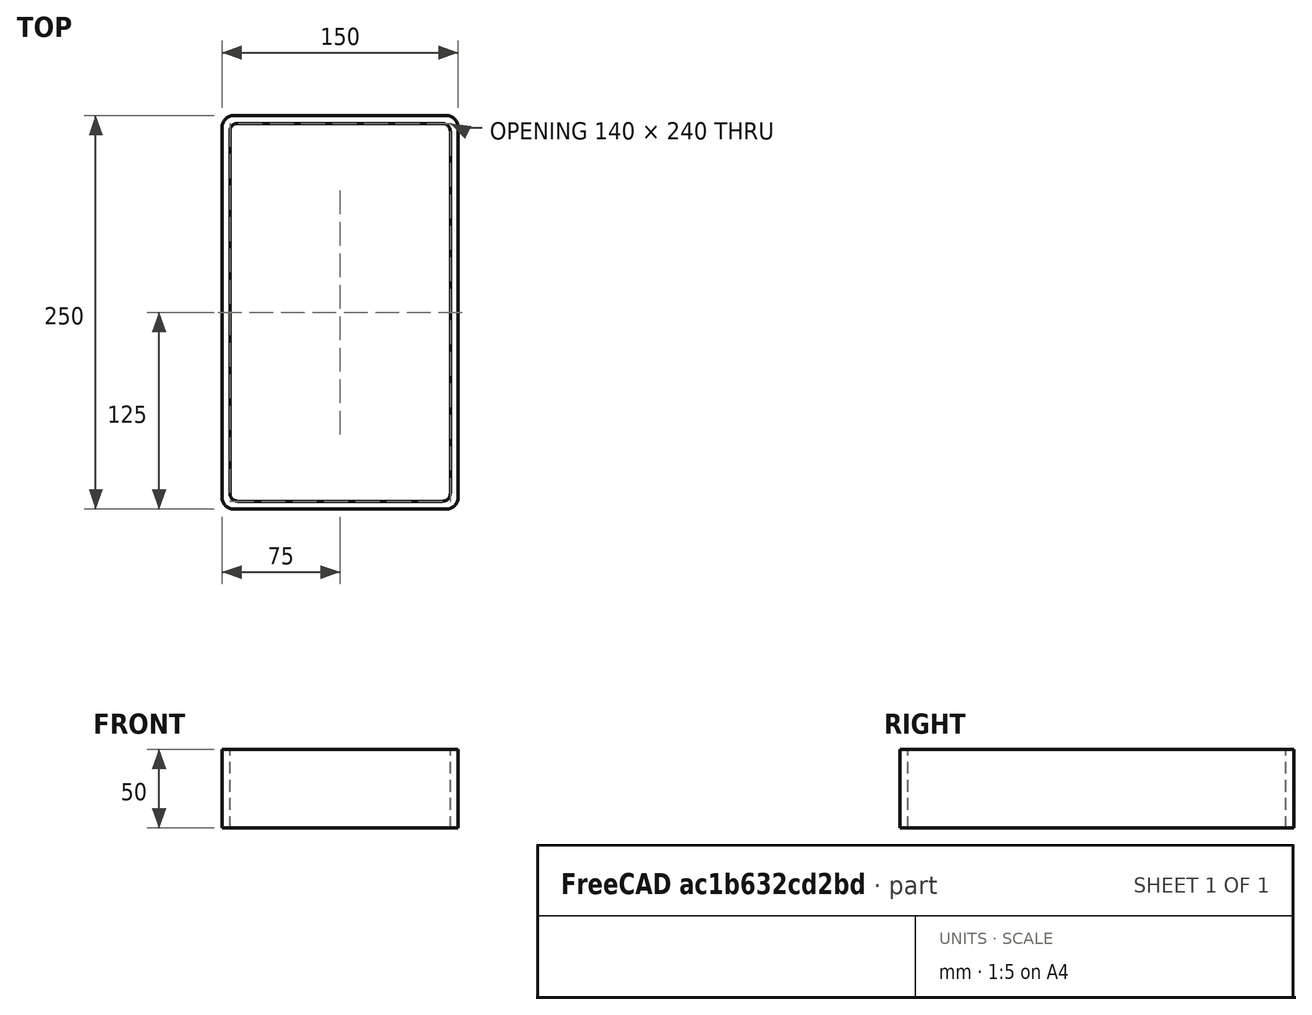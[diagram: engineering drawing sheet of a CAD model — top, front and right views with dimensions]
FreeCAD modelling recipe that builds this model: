
FCSTD DOCUMENT  (FreeCAD 0.15R4671 (Git))
Label: Rectangular hollow section 250x150x5 EN10219 S235JRH
License: All rights reserved
LicenseURL: http://en.wikipedia.org/wiki/All_rights_reserved
objects: Sketcher::SketchObject×1, Part::Extrusion×1
note: 2 computed .brp shape members not serialized (recipe doc carries the construction recipe); baked Part::Feature solids carry a one-line shape summary decoded from their .brp

FEATURE [Sketcher::SketchObject] Sketch
  sketch-geometry (16):
    g0: LineSegment StartX=-65 StartY=120 StartZ=0 EndX=65 EndY=120 EndZ=0
    g1: LineSegment StartX=70 StartY=115 StartZ=0 EndX=70 EndY=-115 EndZ=0
    g2: LineSegment StartX=65 StartY=-120 StartZ=0 EndX=-65 EndY=-120 EndZ=0
    g3: LineSegment StartX=-70 StartY=-115 StartZ=0 EndX=-70 EndY=115 EndZ=0
    g4: LineSegment StartX=-67.5 StartY=125 StartZ=0 EndX=67.5 EndY=125 EndZ=0
    g5: LineSegment StartX=75 StartY=117.5 StartZ=0 EndX=75 EndY=-117.5 EndZ=0
    g6: LineSegment StartX=67.5 StartY=-125 StartZ=0 EndX=-67.5 EndY=-125 EndZ=0
    g7: LineSegment StartX=-75 StartY=-117.5 StartZ=0 EndX=-75 EndY=117.5 EndZ=0
    g8: ArcOfCircle CenterX=-65 CenterY=115 CenterZ=0 NormalX=0 NormalY=0 NormalZ=1 Radius=5 StartAngle=1.5708 EndAngle=3.14159
    g9: ArcOfCircle CenterX=65 CenterY=115 CenterZ=0 NormalX=0 NormalY=0 NormalZ=1 Radius=5 StartAngle=0 EndAngle=1.5708
    g10: ArcOfCircle CenterX=65 CenterY=-115 CenterZ=0 NormalX=0 NormalY=0 NormalZ=1 Radius=5 StartAngle=4.71239 EndAngle=6.28319
    g11: ArcOfCircle CenterX=-65 CenterY=-115 CenterZ=0 NormalX=0 NormalY=0 NormalZ=1 Radius=5 StartAngle=3.14159 EndAngle=4.71239
    g12: ArcOfCircle CenterX=67.5 CenterY=117.5 CenterZ=0 NormalX=0 NormalY=0 NormalZ=1 Radius=7.5 StartAngle=0 EndAngle=1.5708
    g13: ArcOfCircle CenterX=67.5 CenterY=-117.5 CenterZ=0 NormalX=0 NormalY=0 NormalZ=1 Radius=7.5 StartAngle=4.71239 EndAngle=6.28319
    g14: ArcOfCircle CenterX=-67.5 CenterY=-117.5 CenterZ=0 NormalX=0 NormalY=0 NormalZ=1 Radius=7.5 StartAngle=3.14159 EndAngle=4.71239
    g15: ArcOfCircle CenterX=-67.5 CenterY=117.5 CenterZ=0 NormalX=0 NormalY=0 NormalZ=1 Radius=7.5 StartAngle=1.5708 EndAngle=3.14159
  constraints (36):
    c: Horizontal(g2)
    c: Vertical(g3)
    c: Horizontal(g6)
    c: Vertical(g7)
    c: Tangent(g3,g8) = 1.5708
    c: Tangent(g0,g8) = 1.5708
    c: Tangent(g0,g9) = 1.5708
    c: Tangent(g1,g9) = 1.5708
    c: Tangent(g1,g10) = 1.5708
    c: Tangent(g2,g10) = 1.5708
    c: Tangent(g2,g11) = 1.5708
    c: Tangent(g3,g11) = 1.5708
    c: Tangent(g4,g12) = 1.5708
    c: Tangent(g5,g12) = 1.5708
    c: Tangent(g5,g13) = 1.5708
    c: Tangent(g6,g13) = 1.5708
    c: Tangent(g6,g14) = 1.5708
    c: Tangent(g7,g14) = 1.5708
    c: Tangent(g7,g15) = 1.5708
    c: Tangent(g4,g15) = 1.5708
    c: Equal(g9,g8)
    c: Equal(g9,g11)
    c: Equal(g9,g10)
    c: Equal(g12,g15)
    c: Equal(g12,g14)
    c: Equal(g12,g13)
    c: Symmetric(g4,g6,g-1)
    c: Symmetric(g7,g5,g-2)
    c: DistanceY(g4,g6) = -250
    c: DistanceX(g7,g5) = 150
    c: Symmetric(g3,g1,g-2)
    c: Symmetric(g0,g2,g-1)
    c: DistanceY(g0,g4) = 5
    c: DistanceX(g5,g1) = -5
    c: Radius(g9) = 5
    c: Radius(g12) = 7.5
FEATURE [Part::Extrusion] Extrude  label="Rectangular hollow section 250x150x5 EN10219 S235JRH"
  Base = -> Sketch
  Dir = (0,0,50)
  Solid = true
